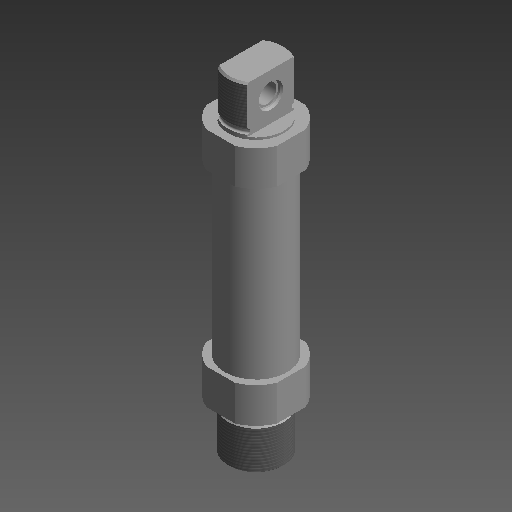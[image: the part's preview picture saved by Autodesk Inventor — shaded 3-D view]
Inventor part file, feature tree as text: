
AUTODESK INVENTOR PART (.ipt)
format: ipt  version: 2021 (Build 250183000, 183)  size: 278,016 bytes
history: native  units: mm (DEFAULTED — no unit token found)
features: other x70, sketch x7, revolve x3, thread x2, extrude x2, hole x2
ambient origin geometry x8: Origin, YZ Plane, XZ Plane, XY Plane, X Axis, Y Axis, Z Axis, Center Point
bodies: Solid1 (feature_tree)
feature tree (86):
  revolve  "Revolution1"  [1 undecoded]
  thread  "Thread1"  [1 undecoded]
  thread  "Thread2"  [1 undecoded]
  extrude  "Extrusion1"  TaperAngle=360.0deg  [1 undecoded]
  extrude  "Extrusion2"  TaperAngle=360.0deg  [1 undecoded]
  revolve  "Revolution2"  [1 undecoded]
  hole  "Hole1"  [1 undecoded]
  hole  "Hole2"  [1 undecoded]
  revolve  "Revolution3"  [1 undecoded]
  other  "FDT_FRONT_XY"
  other  "FDT_FRONT_YZ"
  other  "FDT_FRONT_ZX"
  other  "FDT_FRONT_X"
  other  "FDT_FRONT_Y"
  other  "FDT_FRONT_Z"
  other  "FDT_FRONT_Center"
  other  "FDT_QSFRONT_XY"
  other  "FDT_QSFRONT_YZ"
  other  "FDT_QSFRONT_ZX"
  other  "FDT_QSFRONT_X"
  other  "FDT_QSFRONT_Y"
  other  "FDT_QSFRONT_Z"
  other  "FDT_QSFRONT_Center"
  other  "FDT_QSREAR_XY"
  other  "FDT_QSREAR_YZ"
  other  "FDT_QSREAR_ZX"
  other  "FDT_QSREAR_X"
  other  "FDT_QSREAR_Y"
  other  "FDT_QSREAR_Z"
  other  "FDT_QSREAR_Center"
  other  "FDT_REAR_XY"
  other  "FDT_REAR_YZ"
  other  "FDT_REAR_ZX"
  other  "FDT_REAR_X"
  other  "FDT_REAR_Y"
  other  "FDT_REAR_Z"
  other  "FDT_REAR_Center"
  other  "FDT_SMBR1_XY"
  other  "FDT_SMBR1_YZ"
  other  "FDT_SMBR1_ZX"
  other  "FDT_SMBR1_X"
  other  "FDT_SMBR1_Y"
  other  "FDT_SMBR1_Z"
  other  "FDT_SMBR1_Center"
  other  "FDT_SMBR2_XY"
  other  "FDT_SMBR2_YZ"
  other  "FDT_SMBR2_ZX"
  other  "FDT_SMBR2_X"
  other  "FDT_SMBR2_Y"
  other  "FDT_SMBR2_Z"
  other  "FDT_SMBR2_Center"
  other  "FDT_SWIVELAXIS_XY"
  other  "FDT_SWIVELAXIS_YZ"
  other  "FDT_SWIVELAXIS_ZX"
  other  "FDT_SWIVELAXIS_X"
  other  "FDT_SWIVELAXIS_Y"
  other  "FDT_SWIVELAXIS_Z"
  other  "FDT_SWIVELAXIS_Center"
  other  "NUT_XY"
  other  "NUT_YZ"
  other  "NUT_ZX"
  other  "NUT_X"
  other  "NUT_Y"
  other  "NUT_Z"
  other  "NUT_Center"
  other  "ZR_XY"
  other  "ZR_YZ"
  other  "ZR_ZX"
  other  "ZR_X"
  other  "ZR_Y"
  other  "ZR_Z"
  other  "ZR_Center"
  other  "ZYL_XY"
  other  "ZYL_YZ"
  other  "ZYL_ZX"
  other  "ZYL_X"
  other  "ZYL_Y"
  other  "ZYL_Z"
  other  "ZYL_Center"
  sketch  "Sketch_12"  dims[d25=0.0mm d26=0.0mm]
  sketch  "Sketch_1"  dims[d0=360.0deg d1=20.03mm d2=0.0mm d3=20.03mm d4=0.0mm d5=189.5mm d6=0.0mm]
  sketch  "Sketch_124"  dims[d27=0.0mm d28=0.0mm]
  sketch  "Sketch_3"  dims[d7=38.0mm d8=0.0mm d9=360.0deg]
  sketch  "Sketch5"  dims[d10=8.566mm d11=13.581mm d12=9.728mm d13=2.0mm d14=90.0deg d15=19.0mm d16=0.0mm]
  sketch  "Sketch6"  dims[d17=8.566mm d18=7.581mm d19=9.728mm d20=2.0mm d21=90.0deg d22=8.5mm d23=120.0deg d24=360.0deg]
  sketch  "Sketch_129"  dims[d29=0.0mm d30=0.0mm]
note: 9 required parameter values undecoded (feature->parameter linkage not recoverable at this tier; creation-order binding heuristic only, values carry confidence <= 0.55)